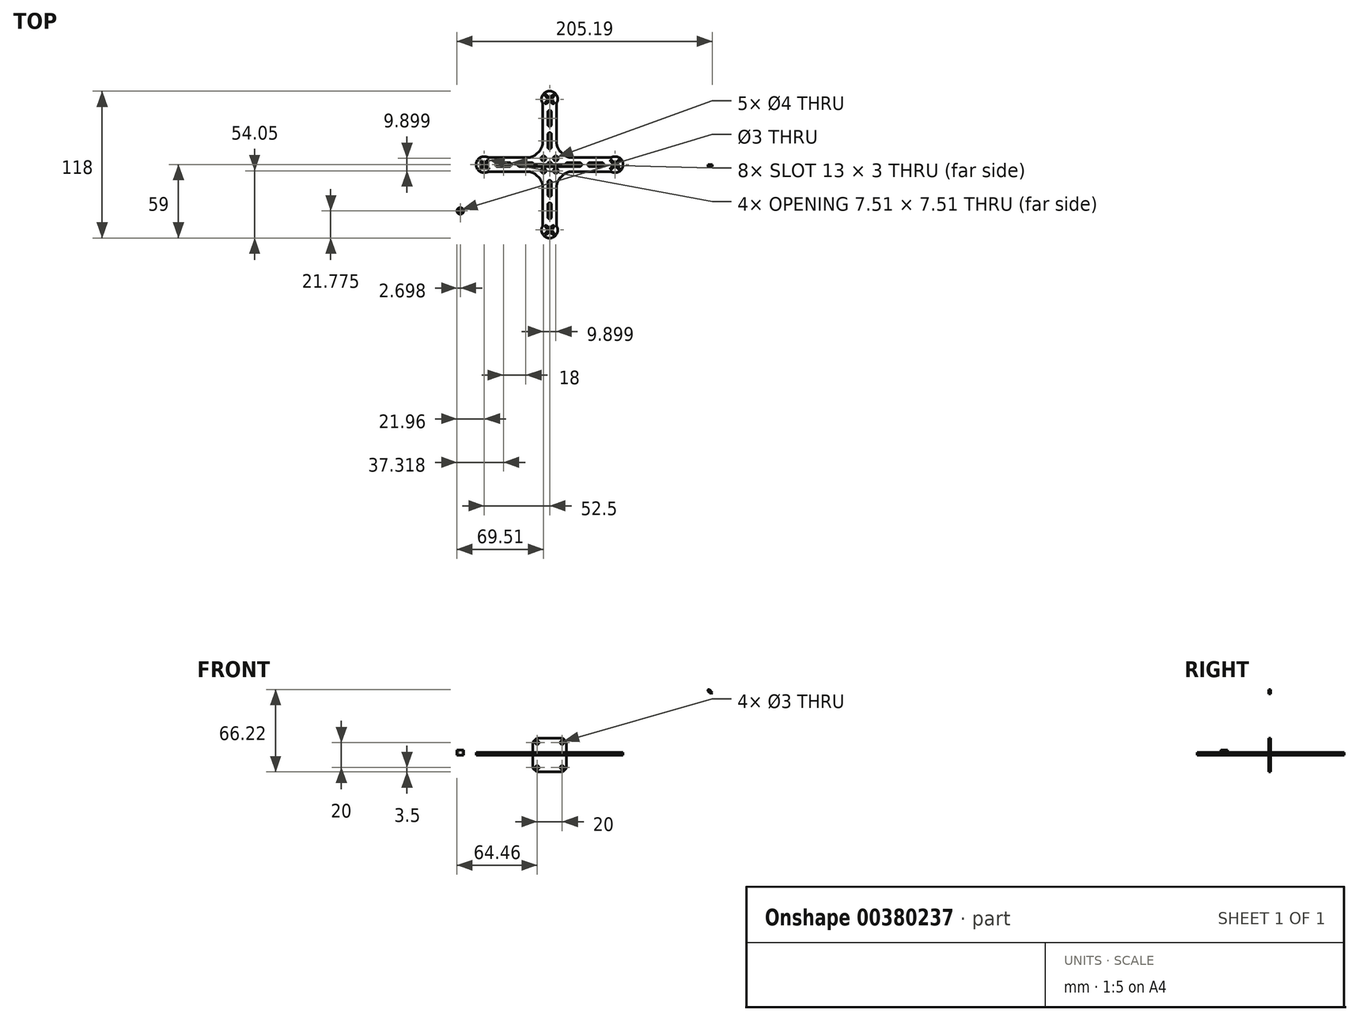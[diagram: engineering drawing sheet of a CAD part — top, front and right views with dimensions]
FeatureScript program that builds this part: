
annotation { "Feature Type Name" : "Feature", "Feature Type Description" : "" }
export const myFeature = defineFeature(function(context is Context, id is Id, definition is map)
    precondition{}
    {
        {
            var Q0;
            Q0=qCreatedBy(makeId("Front.planeOp"),FACE);
            var sketch = newSketch(context, id + "F0", { "sketchPlane" : qUnion([Q0])});
            skCircle(sketch, "E0", {"center": v(-10, 10) * mm, "radius": 1.5 * mm});
            skCircle(sketch, "E1.MirrorC", {"center": v(10, 10) * mm, "radius": 1.5 * mm});
            skCircle(sketch, "E2.MirrorC", {"center": v(-10, -10) * mm, "radius": 1.5 * mm});
            skCircle(sketch, "E3.MirrorC", {"center": v(10, -10) * mm, "radius": 1.5 * mm});
            skLineSegment(sketch, "E4", {"start": v(-13.5, 10.5) * mm, "end": v(-10.5, 13.5) * mm});
            skLineSegment(sketch, "E5", {"start": v(0, 3.77) * mm, "end": v(0, -2.66) * mm, "construction": true});
            skLineSegment(sketch, "E6", {"start": v(-3.53, 0) * mm, "end": v(2.6, 0) * mm, "construction": true});
            skLineSegment(sketch, "E7.MirrorCS", {"start": v(13.5, 10.5) * mm, "end": v(10.5, 13.5) * mm});
            skLineSegment(sketch, "E8.MirrorCS", {"start": v(13.5, -10.5) * mm, "end": v(10.5, -13.5) * mm});
            skLineSegment(sketch, "E9.MirrorCS", {"start": v(-13.5, -10.5) * mm, "end": v(-10.5, -13.5) * mm});
            skLineSegment(sketch, "E10", {"start": v(-13.5, 10.5) * mm, "end": v(-13.5, -10.5) * mm});
            skLineSegment(sketch, "E11", {"start": v(-10.5, 13.5) * mm, "end": v(10.5, 13.5) * mm});
            skLineSegment(sketch, "E12", {"start": v(13.5, 10.5) * mm, "end": v(13.5, -10.5) * mm});
            skLineSegment(sketch, "E13", {"start": v(10.5, -13.5) * mm, "end": v(-10.5, -13.5) * mm});
            skPoint(sketch, "E14.startSnap0", {"position": v(130.73, -3.54) * mm});
            skLineSegment(sketch, "E15", {"start": v(130.73, 48.96) * mm, "end": v(121.15, 39.38) * mm, "construction": true});
            skLineSegment(sketch, "E16", {"start": v(130.73, 48.96) * mm, "end": v(120.31, 59.39) * mm, "construction": true});
            skLineSegment(sketch, "E17", {"start": v(130.73, 48.96) * mm, "end": v(141.05, 59.28) * mm, "construction": true});
            skLineSegment(sketch, "E18", {"start": v(130.73, 48.96) * mm, "end": v(140.68, 39.01) * mm, "construction": true});
            skCircle(sketch, "E19", {"center": v(130.73, 48.96) * mm, "radius": 4.25 * mm, "construction": true});
            skLineSegment(sketch, "E20", {"start": v(128.26, 52.5) * mm, "end": v(134.27, 46.49) * mm});
            skLineSegment(sketch, "E21", {"start": v(127.2, 51.44) * mm, "end": v(133.2, 45.43) * mm});
            skLineSegment(sketch, "E22", {"start": v(127.2, 46.49) * mm, "end": v(133.16, 52.45) * mm});
            skLineSegment(sketch, "E23", {"start": v(134.27, 51.44) * mm, "end": v(128.26, 45.43) * mm});
            skArc(sketch, "E24", {"start": v(127.2, 51.44) * mm, "mid": v(127.2, 52.5) * mm, "end": v(128.26, 52.5) * mm});
            skArc(sketch, "E25", {"start": v(134.27, 46.49) * mm, "mid": v(134.27, 45.43) * mm, "end": v(133.2, 45.43) * mm});
            skArc(sketch, "E26", {"start": v(128.26, 45.43) * mm, "mid": v(127.2, 45.43) * mm, "end": v(127.2, 46.49) * mm});
            skArc(sketch, "E27", {"start": v(133.16, 52.45) * mm, "mid": v(134.24, 52.52) * mm, "end": v(134.27, 51.44) * mm});
            skLineSegment(sketch, "E28", {"start": v(130.73, 48.96) * mm, "end": v(121.92, 48.96) * mm, "construction": true});
            skLineSegment(sketch, "E29", {"start": v(130.73, 48.96) * mm, "end": v(139.92, 48.96) * mm, "construction": true});
            skLineSegment(sketch, "E30", {"start": v(130.73, -3.54) * mm, "end": v(147.32, 13.05) * mm, "construction": true});
            skLineSegment(sketch, "E31", {"start": v(130.73, -3.54) * mm, "end": v(114.8, -19.47) * mm, "construction": true});
            skLineSegment(sketch, "E32", {"start": v(130.73, -3.54) * mm, "end": v(113.54, 13.66) * mm, "construction": true});
            skLineSegment(sketch, "E33", {"start": v(130.73, -3.54) * mm, "end": v(149.26, -22.06) * mm, "construction": true});
            skPoint(sketch, "E34.centerSnap0", {"position": v(141.34, 7.07) * mm});
            skLineSegment(sketch, "E35", {"start": v(130.73, 35.6) * mm, "end": v(133.9, 35.6) * mm, "construction": true});
            skPoint(sketch, "E36.startSnap0", {"position": v(132.32, 35.6) * mm});
            skLineSegment(sketch, "E37", {"start": v(130.73, 10.6) * mm, "end": v(134.35, 10.6) * mm, "construction": true});
            skArc(sketch, "E38", {"start": v(132.23, 35.6) * mm, "mid": v(130.73, 37.1) * mm, "end": v(129.23, 35.6) * mm});
            skArc(sketch, "E39", {"start": v(132.23, 10.6) * mm, "mid": v(130.73, 9.1) * mm, "end": v(129.23, 10.6) * mm});
            skLineSegment(sketch, "E40", {"start": v(130.73, 48.96) * mm, "end": v(121.76, 43.79) * mm, "construction": true});
            skLineSegment(sketch, "E41.MirrorCS", {"start": v(130.73, 48.96) * mm, "end": v(139.7, 43.79) * mm, "construction": true});
            skLineSegment(sketch, "E42", {"start": v(136.36, 45.71) * mm, "end": v(137.16, 47.1) * mm, "construction": true});
            skArc(sketch, "E43", {"start": v(136.36, 45.71) * mm, "mid": v(130.73, 55.46) * mm, "end": v(125.1, 45.71) * mm});
            skLineSegment(sketch, "E44", {"start": v(125.1, 45.71) * mm, "end": v(125.1, 16.2) * mm});
            skLineSegment(sketch, "E45.MirrorCS", {"start": v(136.36, 45.71) * mm, "end": v(136.36, 16.2) * mm});
            skLineSegment(sketch, "E46.1.1", {"start": v(91.6, -5.04) * mm, "end": v(116.6, -5.04) * mm});
            skLineSegment(sketch, "E46.1.2", {"start": v(74.7, -6.01) * mm, "end": v(80.7, 0) * mm});
            skLineSegment(sketch, "E46.1.4", {"start": v(91.6, -2.04) * mm, "end": v(116.6, -2.04) * mm});
            skPoint(sketch, "E46.1.5", {"position": v(120.13, 7.07) * mm});
            skLineSegment(sketch, "E46.1.6", {"start": v(81.48, 2.1) * mm, "end": v(111, 2.1) * mm});
            skLineSegment(sketch, "E46.1.7", {"start": v(81.48, -9.16) * mm, "end": v(111, -9.16) * mm});
            skLineSegment(sketch, "E46.1.8", {"start": v(75.76, -7.07) * mm, "end": v(81.77, -1.06) * mm});
            skLineSegment(sketch, "E46.1.10", {"start": v(75.76, 0) * mm, "end": v(81.77, -6.01) * mm});
            skPoint(sketch, "E46.1.12", {"position": v(91.6, -1.95) * mm});
            skArc(sketch, "E46.1.14", {"start": v(81.48, 2.1) * mm, "mid": v(71.73, -3.54) * mm, "end": v(81.48, -9.16) * mm});
            skArc(sketch, "E46.1.20", {"start": v(74.75, -1.1) * mm, "mid": v(74.67, -0.02) * mm, "end": v(75.76, 0) * mm});
            skLineSegment(sketch, "E46.1.21", {"start": v(80.7, -7.07) * mm, "end": v(74.75, -1.1) * mm});
            skArc(sketch, "E46.1.22", {"start": v(116.6, -2.04) * mm, "mid": v(118.1, -3.54) * mm, "end": v(116.6, -5.04) * mm});
            skArc(sketch, "E46.1.23", {"start": v(81.77, -6.01) * mm, "mid": v(81.77, -7.07) * mm, "end": v(80.7, -7.07) * mm});
            skArc(sketch, "E46.1.24", {"start": v(75.76, -7.07) * mm, "mid": v(74.7, -7.07) * mm, "end": v(74.7, -6.01) * mm});
            skArc(sketch, "E46.1.26", {"start": v(91.6, -2.04) * mm, "mid": v(90.1, -3.54) * mm, "end": v(91.6, -5.04) * mm});
            skArc(sketch, "E46.1.27", {"start": v(80.7, 0) * mm, "mid": v(81.77, 0) * mm, "end": v(81.77, -1.06) * mm});
            skLineSegment(sketch, "E46.2.1", {"start": v(132.23, -42.68) * mm, "end": v(132.23, -17.68) * mm});
            skLineSegment(sketch, "E46.2.2", {"start": v(133.2, -59.57) * mm, "end": v(127.2, -53.56) * mm});
            skLineSegment(sketch, "E46.2.4", {"start": v(129.23, -42.68) * mm, "end": v(129.23, -17.68) * mm});
            skPoint(sketch, "E46.2.5", {"position": v(120.13, -14.14) * mm});
            skLineSegment(sketch, "E46.2.6", {"start": v(125.1, -52.79) * mm, "end": v(125.1, -23.26) * mm});
            skLineSegment(sketch, "E46.2.7", {"start": v(136.36, -52.79) * mm, "end": v(136.36, -23.26) * mm});
            skLineSegment(sketch, "E46.2.8", {"start": v(134.27, -58.51) * mm, "end": v(128.26, -52.5) * mm});
            skLineSegment(sketch, "E46.2.10", {"start": v(127.2, -58.51) * mm, "end": v(133.2, -52.5) * mm});
            skPoint(sketch, "E46.2.12", {"position": v(129.15, -42.68) * mm});
            skArc(sketch, "E46.2.14", {"start": v(125.1, -52.79) * mm, "mid": v(130.73, -62.54) * mm, "end": v(136.36, -52.79) * mm});
            skArc(sketch, "E46.2.20", {"start": v(128.3, -59.52) * mm, "mid": v(127.22, -59.6) * mm, "end": v(127.2, -58.51) * mm});
            skLineSegment(sketch, "E46.2.21", {"start": v(134.27, -53.56) * mm, "end": v(128.3, -59.52) * mm});
            skArc(sketch, "E46.2.22", {"start": v(129.23, -17.68) * mm, "mid": v(130.73, -16.18) * mm, "end": v(132.23, -17.68) * mm});
            skArc(sketch, "E46.2.23", {"start": v(133.2, -52.5) * mm, "mid": v(134.27, -52.5) * mm, "end": v(134.27, -53.56) * mm});
            skArc(sketch, "E46.2.24", {"start": v(134.27, -58.51) * mm, "mid": v(134.27, -59.57) * mm, "end": v(133.2, -59.57) * mm});
            skArc(sketch, "E46.2.26", {"start": v(129.23, -42.68) * mm, "mid": v(130.73, -44.18) * mm, "end": v(132.23, -42.68) * mm});
            skArc(sketch, "E46.2.27", {"start": v(127.2, -53.56) * mm, "mid": v(127.2, -52.5) * mm, "end": v(128.26, -52.5) * mm});
            skLineSegment(sketch, "E46.3.1", {"start": v(169.88, -2.04) * mm, "end": v(144.88, -2.04) * mm});
            skLineSegment(sketch, "E46.3.2", {"start": v(186.77, -1.06) * mm, "end": v(180.76, -7.07) * mm});
            skLineSegment(sketch, "E46.3.4", {"start": v(169.88, -5.04) * mm, "end": v(144.88, -5.04) * mm});
            skPoint(sketch, "E46.3.5", {"position": v(141.34, -14.14) * mm});
            skLineSegment(sketch, "E46.3.6", {"start": v(179.98, -9.16) * mm, "end": v(150.46, -9.16) * mm});
            skLineSegment(sketch, "E46.3.7", {"start": v(179.98, 2.1) * mm, "end": v(150.46, 2.1) * mm});
            skLineSegment(sketch, "E46.3.8", {"start": v(185.7, 0) * mm, "end": v(179.7, -6.01) * mm});
            skLineSegment(sketch, "E46.3.10", {"start": v(185.7, -7.07) * mm, "end": v(179.7, -1.06) * mm});
            skPoint(sketch, "E46.3.12", {"position": v(169.88, -5.12) * mm});
            skArc(sketch, "E46.3.14", {"start": v(179.98, -9.16) * mm, "mid": v(189.73, -3.54) * mm, "end": v(179.98, 2.1) * mm});
            skArc(sketch, "E46.3.20", {"start": v(186.72, -5.97) * mm, "mid": v(186.8, -7.05) * mm, "end": v(185.7, -7.07) * mm});
            skLineSegment(sketch, "E46.3.21", {"start": v(180.76, 0) * mm, "end": v(186.72, -5.97) * mm});
            skArc(sketch, "E46.3.22", {"start": v(144.88, -5.04) * mm, "mid": v(143.38, -3.54) * mm, "end": v(144.88, -2.04) * mm});
            skArc(sketch, "E46.3.23", {"start": v(179.7, -1.06) * mm, "mid": v(179.7, 0) * mm, "end": v(180.76, 0) * mm});
            skArc(sketch, "E46.3.24", {"start": v(185.7, 0) * mm, "mid": v(186.77, 0) * mm, "end": v(186.77, -1.06) * mm});
            skArc(sketch, "E46.3.26", {"start": v(169.88, -5.04) * mm, "mid": v(171.38, -3.54) * mm, "end": v(169.88, -2.04) * mm});
            skArc(sketch, "E46.3.27", {"start": v(180.76, -7.07) * mm, "mid": v(179.7, -7.07) * mm, "end": v(179.7, -6.01) * mm});
            skLineSegment(sketch, "E47", {"start": v(122.18, 9.12) * mm, "end": v(118.08, 5.02) * mm});
            skLineSegment(sketch, "E48", {"start": v(118.08, -12.1) * mm, "end": v(122.18, -16.2) * mm});
            skLineSegment(sketch, "E49", {"start": v(139.3, -16.2) * mm, "end": v(143.39, -12.1) * mm});
            skLineSegment(sketch, "E50", {"start": v(143.39, 5.02) * mm, "end": v(139.3, 9.12) * mm});
            skArc(sketch, "E51.filletArc", {"start": v(122.18, 9.12) * mm, "mid": v(124.34, 12.36) * mm, "end": v(125.1, 16.2) * mm});
            skPoint(sketch, "E52.visualSharp", {"position": v(115.15, 2.1) * mm});
            skArc(sketch, "E52.filletArc", {"start": v(111, 2.1) * mm, "mid": v(114.83, 2.85) * mm, "end": v(118.08, 5.02) * mm});
            skPoint(sketch, "E53.visualSharp", {"position": v(136.36, 12.05) * mm});
            skArc(sketch, "E53.filletArc", {"start": v(136.36, 16.2) * mm, "mid": v(137.12, 12.36) * mm, "end": v(139.3, 9.12) * mm});
            skArc(sketch, "E54.filletArc", {"start": v(143.39, 5.02) * mm, "mid": v(146.63, 2.85) * mm, "end": v(150.46, 2.1) * mm});
            skPoint(sketch, "E55.visualSharp", {"position": v(146.32, -9.16) * mm});
            skArc(sketch, "E55.filletArc", {"start": v(150.46, -9.16) * mm, "mid": v(146.63, -9.93) * mm, "end": v(143.39, -12.1) * mm});
            skArc(sketch, "E56.filletArc", {"start": v(139.3, -16.2) * mm, "mid": v(137.12, -19.43) * mm, "end": v(136.36, -23.26) * mm});
            skPoint(sketch, "E57.visualSharp", {"position": v(125.1, -19.12) * mm});
            skArc(sketch, "E57.filletArc", {"start": v(125.1, -23.26) * mm, "mid": v(124.34, -19.43) * mm, "end": v(122.18, -16.2) * mm});
            skArc(sketch, "E58.filletArc", {"start": v(118.08, -12.1) * mm, "mid": v(114.83, -9.93) * mm, "end": v(111, -9.16) * mm});
            skCircle(sketch, "E59", {"center": v(130.73, -3.54) * mm, "radius": 2 * mm});
            skCircle(sketch, "E60", {"center": v(136.39, 2.12) * mm, "radius": 2 * mm});
            skCircle(sketch, "E61.MirrorC", {"center": v(125.08, -9.2) * mm, "radius": 2 * mm});
            skLineSegment(sketch, "E62", {"start": v(130.73, -3.54) * mm, "end": v(130.73, 5.88) * mm, "construction": true});
            skCircle(sketch, "E63.MirrorC", {"center": v(125.08, 2.12) * mm, "radius": 2 * mm});
            skCircle(sketch, "E64.MirrorC", {"center": v(136.39, -9.2) * mm, "radius": 2 * mm});
            skLineSegment(sketch, "E65", {"start": v(129.23, 35.6) * mm, "end": v(129.23, 27.6) * mm});
            skLineSegment(sketch, "E66", {"start": v(132.23, 27.6) * mm, "end": v(132.23, 35.6) * mm});
            skLineSegment(sketch, "E67", {"start": v(129.23, 10.6) * mm, "end": v(129.23, 18.6) * mm});
            skLineSegment(sketch, "E68", {"start": v(132.23, 18.6) * mm, "end": v(132.23, 10.6) * mm});
            skArc(sketch, "E69", {"start": v(129.23, 18.6) * mm, "mid": v(130.73, 20.1) * mm, "end": v(132.23, 18.6) * mm});
            skArc(sketch, "E70", {"start": v(129.23, 27.6) * mm, "mid": v(130.73, 26.1) * mm, "end": v(132.23, 27.6) * mm});
            skCircle(sketch, "E71", {"center": v(252.65, 46.38) * mm, "radius": 4.25 * mm, "construction": true});
            skLineSegment(sketch, "E72", {"start": v(245.3, 46.38) * mm, "end": v(259.84, 46.38) * mm, "construction": true});
            skLineSegment(sketch, "E73", {"start": v(252.65, 46.38) * mm, "end": v(246.48, 40.2) * mm, "construction": true});
            skLineSegment(sketch, "E74", {"start": v(252.65, 46.38) * mm, "end": v(258.2, 51.93) * mm, "construction": true});
            skLineSegment(sketch, "E75.MirrorCS", {"start": v(252.65, 46.38) * mm, "end": v(247.1, 51.93) * mm, "construction": true});
            skLineSegment(sketch, "E76", {"start": v(254.27, 49.06) * mm, "end": v(249.97, 44.76) * mm, "construction": true});
            skLineSegment(sketch, "E77", {"start": v(249.65, 49.38) * mm, "end": v(248.95, 48.68) * mm, "construction": true});
            skLineSegment(sketch, "E78", {"start": v(249.12, 48.85) * mm, "end": v(251.6, 46.38) * mm});
            skLineSegment(sketch, "E79.MirrorCS", {"start": v(250.18, 49.91) * mm, "end": v(252.65, 47.44) * mm});
            skArc(sketch, "E80", {"start": v(249.12, 48.85) * mm, "mid": v(249.12, 49.91) * mm, "end": v(250.18, 49.91) * mm});
            skArc(sketch, "E81.1.0", {"start": v(250.18, 42.84) * mm, "mid": v(249.12, 42.84) * mm, "end": v(249.12, 43.9) * mm});
            skLineSegment(sketch, "E81.1.1", {"start": v(249.12, 43.9) * mm, "end": v(251.6, 46.38) * mm});
            skLineSegment(sketch, "E81.1.2", {"start": v(250.18, 42.84) * mm, "end": v(252.65, 45.32) * mm});
            skArc(sketch, "E81.2.0", {"start": v(256.19, 43.9) * mm, "mid": v(256.19, 42.84) * mm, "end": v(255.13, 42.84) * mm});
            skLineSegment(sketch, "E81.2.1", {"start": v(255.13, 42.84) * mm, "end": v(252.65, 45.32) * mm});
            skLineSegment(sketch, "E81.2.2", {"start": v(256.19, 43.9) * mm, "end": v(253.71, 46.38) * mm});
            skArc(sketch, "E81.3.0", {"start": v(255.13, 49.91) * mm, "mid": v(256.19, 49.91) * mm, "end": v(256.19, 48.85) * mm});
            skLineSegment(sketch, "E81.3.1", {"start": v(256.19, 48.85) * mm, "end": v(253.71, 46.38) * mm});
            skLineSegment(sketch, "E81.3.2", {"start": v(255.13, 49.91) * mm, "end": v(252.65, 47.44) * mm});
            skLineSegment(sketch, "E82", {"start": v(252.65, 46.38) * mm, "end": v(246.46, 42.8) * mm, "construction": true});
            skLineSegment(sketch, "E83.MirrorCS", {"start": v(252.65, 46.38) * mm, "end": v(258.84, 42.8) * mm, "construction": true});
            skArc(sketch, "E84", {"start": v(247.02, 43.13) * mm, "mid": v(252.65, 52.88) * mm, "end": v(258.28, 43.13) * mm});
            skCircle(sketch, "E85", {"center": v(252.65, -6.12) * mm, "radius": 2 * mm});
            skLineSegment(sketch, "E86", {"start": v(252.65, 57.43) * mm, "end": v(252.65, -10.81) * mm, "construction": true});
            skCircle(sketch, "E87", {"center": v(252.65, 8.02) * mm, "radius": 1.5 * mm, "construction": true});
            skCircle(sketch, "E88", {"center": v(252.65, 36.02) * mm, "radius": 1.5 * mm, "construction": true});
            skCircle(sketch, "E89", {"center": v(252.65, 26.02) * mm, "radius": 1.5 * mm, "construction": true});
            skCircle(sketch, "E90", {"center": v(252.65, 18.02) * mm, "radius": 1.5 * mm, "construction": true});
            skLineSegment(sketch, "E91", {"start": v(251.15, 18.02) * mm, "end": v(251.15, 8.02) * mm});
            skLineSegment(sketch, "E92", {"start": v(254.15, 18.02) * mm, "end": v(254.15, 8.02) * mm});
            skArc(sketch, "E93", {"start": v(251.15, 8.02) * mm, "mid": v(252.65, 6.52) * mm, "end": v(254.15, 8.02) * mm});
            skArc(sketch, "E94", {"start": v(251.15, 18.02) * mm, "mid": v(252.65, 19.52) * mm, "end": v(254.15, 18.02) * mm});
            skLineSegment(sketch, "E95", {"start": v(251.15, 26.02) * mm, "end": v(251.15, 36.02) * mm});
            skLineSegment(sketch, "E96", {"start": v(254.15, 36.02) * mm, "end": v(254.15, 26.02) * mm});
            skArc(sketch, "E97", {"start": v(251.15, 26.02) * mm, "mid": v(252.65, 24.52) * mm, "end": v(254.15, 26.02) * mm});
            skArc(sketch, "E98", {"start": v(251.15, 36.02) * mm, "mid": v(252.65, 37.52) * mm, "end": v(254.15, 36.02) * mm});
            skLineSegment(sketch, "E99", {"start": v(252.65, -6.12) * mm, "end": v(265.9, 7.13) * mm, "construction": true});
            skLineSegment(sketch, "E100", {"start": v(252.65, -6.12) * mm, "end": v(239.95, -18.82) * mm, "construction": true});
            skLineSegment(sketch, "E101.MirrorCS", {"start": v(252.65, -6.12) * mm, "end": v(239.4, 7.13) * mm, "construction": true});
            skLineSegment(sketch, "E102.MirrorCS", {"start": v(252.65, -6.12) * mm, "end": v(265.35, -18.82) * mm, "construction": true});
            skSolve(sketch);
        }
        {
            var Q0;
            Q0=makeQuery(id+"F0.imprint","IMPRINT",FACE,{"disambiguationData":[TD([[makeQuery(id+"F0.imprint","IMPRINT",EDGE,{"derivedFrom":sQuery(id+"F0.wireOp",EDGE,"E0")}),-1.0]])]});
            var Q1;
            {var subQ28=sQuery(id+"F0.wireOp",EDGE,"E24");Q1=makeQuery(id+"F0.imprint","IMPRINT",FACE,{"disambiguationData":[TD([[makeQuery(id+"F0.imprint","IMPRINT",EDGE,{"derivedFrom":subQ28}),1.0]])]});}
            extrude(context, id + "F1", {"entities" : qUnion([Q0, Q1]), "depth" : 1.5 * mm});
        }
        {
            var Q0;
            Q0=qCreatedBy(makeId("Top.planeOp"),FACE);
            var sketch = newSketch(context, id + "F2", { "sketchPlane" : qUnion([Q0])});
            skCircle(sketch, "E103", {"center": v(0, 52.5) * mm, "radius": 4.25 * mm, "construction": true});
            skLineSegment(sketch, "E104", {"start": v(-7.35, 52.5) * mm, "end": v(7.2, 52.5) * mm, "construction": true});
            skLineSegment(sketch, "E105", {"start": v(0, 52.5) * mm, "end": v(-6.17, 46.33) * mm, "construction": true});
            skLineSegment(sketch, "E106", {"start": v(0, 52.5) * mm, "end": v(5.55, 58.05) * mm, "construction": true});
            skLineSegment(sketch, "E107.MirrorCS", {"start": v(0, 52.5) * mm, "end": v(-5.55, 58.05) * mm, "construction": true});
            skLineSegment(sketch, "E108", {"start": v(-3, 55.5) * mm, "end": v(-3.7, 54.8) * mm, "construction": true});
            skLineSegment(sketch, "E109", {"start": v(-3.54, 54.97) * mm, "end": v(-1.06, 52.5) * mm});
            skLineSegment(sketch, "E110.MirrorCS", {"start": v(-2.47, 56.04) * mm, "end": v(0, 53.56) * mm});
            skArc(sketch, "E111", {"start": v(-3.54, 54.97) * mm, "mid": v(-3.54, 56.04) * mm, "end": v(-2.47, 56.04) * mm});
            skArc(sketch, "E112.1.0", {"start": v(-2.47, 48.96) * mm, "mid": v(-3.54, 48.96) * mm, "end": v(-3.54, 50.03) * mm});
            skLineSegment(sketch, "E112.1.1", {"start": v(-3.54, 50.03) * mm, "end": v(-1.06, 52.5) * mm});
            skLineSegment(sketch, "E112.1.2", {"start": v(-2.47, 48.96) * mm, "end": v(0, 51.44) * mm});
            skArc(sketch, "E112.2.0", {"start": v(3.54, 50.03) * mm, "mid": v(3.54, 48.96) * mm, "end": v(2.47, 48.96) * mm});
            skLineSegment(sketch, "E112.2.1", {"start": v(2.47, 48.96) * mm, "end": v(0, 51.44) * mm});
            skLineSegment(sketch, "E112.2.2", {"start": v(3.54, 50.03) * mm, "end": v(1.06, 52.5) * mm});
            skArc(sketch, "E112.3.0", {"start": v(2.47, 56.04) * mm, "mid": v(3.54, 56.04) * mm, "end": v(3.54, 54.97) * mm});
            skLineSegment(sketch, "E112.3.1", {"start": v(3.54, 54.97) * mm, "end": v(1.06, 52.5) * mm});
            skLineSegment(sketch, "E112.3.2", {"start": v(2.47, 56.04) * mm, "end": v(0, 53.56) * mm});
            skLineSegment(sketch, "E113", {"start": v(0, 52.5) * mm, "end": v(-6.19, 48.93) * mm, "construction": true});
            skLineSegment(sketch, "E114.MirrorCS", {"start": v(0, 52.5) * mm, "end": v(6.19, 48.93) * mm, "construction": true});
            skArc(sketch, "E115", {"start": v(-5.63, 49.25) * mm, "mid": v(0, 59) * mm, "end": v(5.63, 49.25) * mm});
            skCircle(sketch, "E116", {"center": v(0, 0) * mm, "radius": 2 * mm});
            skLineSegment(sketch, "E117", {"start": v(0, 65.69) * mm, "end": v(0, -2.55) * mm, "construction": true});
            skLineSegment(sketch, "E118", {"start": v(-1.5, 24.14) * mm, "end": v(-1.5, 14.14) * mm});
            skLineSegment(sketch, "E119", {"start": v(1.5, 24.14) * mm, "end": v(1.5, 14.14) * mm});
            skArc(sketch, "E120", {"start": v(-1.5, 14.14) * mm, "mid": v(0, 12.64) * mm, "end": v(1.5, 14.14) * mm});
            skArc(sketch, "E121", {"start": v(-1.5, 24.14) * mm, "mid": v(0, 25.64) * mm, "end": v(1.5, 24.14) * mm});
            skLineSegment(sketch, "E122", {"start": v(-1.5, 32.14) * mm, "end": v(-1.5, 42.14) * mm});
            skLineSegment(sketch, "E123", {"start": v(1.5, 42.14) * mm, "end": v(1.5, 32.14) * mm});
            skArc(sketch, "E124", {"start": v(-1.5, 32.14) * mm, "mid": v(0, 30.64) * mm, "end": v(1.5, 32.14) * mm});
            skArc(sketch, "E125", {"start": v(-1.5, 42.14) * mm, "mid": v(0, 43.64) * mm, "end": v(1.5, 42.14) * mm});
            skLineSegment(sketch, "E126", {"start": v(0, 0) * mm, "end": v(13.25, 13.25) * mm, "construction": true});
            skLineSegment(sketch, "E127", {"start": v(0, 0) * mm, "end": v(-12.7, -12.7) * mm, "construction": true});
            skLineSegment(sketch, "E128.MirrorCS", {"start": v(0, 0) * mm, "end": v(-13.25, 13.25) * mm, "construction": true});
            skLineSegment(sketch, "E129.MirrorCS", {"start": v(0, 0) * mm, "end": v(12.7, -12.7) * mm, "construction": true});
            skCircle(sketch, "E130", {"center": v(4.95, 4.95) * mm, "radius": 2 * mm});
            skCircle(sketch, "E131.MirrorC", {"center": v(-4.95, 4.95) * mm, "radius": 2 * mm});
            skCircle(sketch, "E132.MirrorC", {"center": v(4.95, -4.95) * mm, "radius": 2 * mm});
            skCircle(sketch, "E133.MirrorC", {"center": v(-4.95, -4.95) * mm, "radius": 2 * mm});
            skLineSegment(sketch, "E134", {"start": v(-5.63, 49.25) * mm, "end": v(-5.63, 17.6) * mm});
            skLineSegment(sketch, "E135", {"start": v(5.63, 49.25) * mm, "end": v(5.63, 17.6) * mm});
            skCircle(sketch, "E136", {"center": v(-380.04, 55.3) * mm, "radius": 4.25 * mm, "construction": true});
            skLineSegment(sketch, "E137", {"start": v(-387.39, 55.3) * mm, "end": v(-372.84, 55.3) * mm, "construction": true});
            skLineSegment(sketch, "E138", {"start": v(-380.04, 55.3) * mm, "end": v(-386.2, 49.13) * mm, "construction": true});
            skLineSegment(sketch, "E139", {"start": v(-380.04, 55.3) * mm, "end": v(-374.48, 60.86) * mm, "construction": true});
            skLineSegment(sketch, "E140.MirrorCS", {"start": v(-380.04, 55.3) * mm, "end": v(-385.59, 60.86) * mm, "construction": true});
            skLineSegment(sketch, "E141", {"start": v(-378.42, 57.98) * mm, "end": v(-382.72, 53.68) * mm, "construction": true});
            skLineSegment(sketch, "E142", {"start": v(-383.04, 58.3) * mm, "end": v(-383.74, 57.6) * mm, "construction": true});
            skLineSegment(sketch, "E143", {"start": v(-383.57, 57.78) * mm, "end": v(-381.1, 55.3) * mm});
            skLineSegment(sketch, "E144.MirrorCS", {"start": v(-382.51, 58.84) * mm, "end": v(-380.04, 56.36) * mm});
            skArc(sketch, "E145", {"start": v(-383.57, 57.78) * mm, "mid": v(-383.57, 58.84) * mm, "end": v(-382.51, 58.84) * mm});
            skArc(sketch, "E146.1.0", {"start": v(-382.51, 51.77) * mm, "mid": v(-383.57, 51.77) * mm, "end": v(-383.57, 52.83) * mm});
            skLineSegment(sketch, "E146.1.1", {"start": v(-383.57, 52.83) * mm, "end": v(-381.1, 55.3) * mm});
            skLineSegment(sketch, "E146.1.2", {"start": v(-382.51, 51.77) * mm, "end": v(-380.04, 54.24) * mm});
            skArc(sketch, "E146.2.0", {"start": v(-376.5, 52.83) * mm, "mid": v(-376.5, 51.77) * mm, "end": v(-377.56, 51.77) * mm});
            skLineSegment(sketch, "E146.2.1", {"start": v(-377.56, 51.77) * mm, "end": v(-380.04, 54.24) * mm});
            skLineSegment(sketch, "E146.2.2", {"start": v(-376.5, 52.83) * mm, "end": v(-378.98, 55.3) * mm});
            skArc(sketch, "E146.3.0", {"start": v(-377.56, 58.84) * mm, "mid": v(-376.5, 58.84) * mm, "end": v(-376.5, 57.78) * mm});
            skLineSegment(sketch, "E146.3.1", {"start": v(-376.5, 57.78) * mm, "end": v(-378.98, 55.3) * mm});
            skLineSegment(sketch, "E146.3.2", {"start": v(-377.56, 58.84) * mm, "end": v(-380.04, 56.36) * mm});
            skLineSegment(sketch, "E147", {"start": v(-380.04, 55.3) * mm, "end": v(-386.22, 51.73) * mm, "construction": true});
            skLineSegment(sketch, "E148.MirrorCS", {"start": v(-380.04, 55.3) * mm, "end": v(-373.85, 51.73) * mm, "construction": true});
            skArc(sketch, "E149", {"start": v(-385.66, 52.05) * mm, "mid": v(-380.04, 61.8) * mm, "end": v(-374.4, 52.05) * mm});
            skCircle(sketch, "E150", {"center": v(-380.04, 2.8) * mm, "radius": 2 * mm});
            skLineSegment(sketch, "E151", {"start": v(-380.04, 68.5) * mm, "end": v(-380.04, 0.25) * mm, "construction": true});
            skCircle(sketch, "E152", {"center": v(-380.04, 16.95) * mm, "radius": 1.5 * mm, "construction": true});
            skCircle(sketch, "E153", {"center": v(-380.04, 44.95) * mm, "radius": 1.5 * mm, "construction": true});
            skCircle(sketch, "E154", {"center": v(-380.04, 34.95) * mm, "radius": 1.5 * mm, "construction": true});
            skCircle(sketch, "E155", {"center": v(-380.04, 26.95) * mm, "radius": 1.5 * mm, "construction": true});
            skLineSegment(sketch, "E156", {"start": v(-381.54, 26.95) * mm, "end": v(-381.54, 16.95) * mm});
            skLineSegment(sketch, "E157", {"start": v(-378.54, 26.95) * mm, "end": v(-378.54, 16.95) * mm});
            skArc(sketch, "E158", {"start": v(-381.54, 16.95) * mm, "mid": v(-380.04, 15.45) * mm, "end": v(-378.54, 16.95) * mm});
            skArc(sketch, "E159", {"start": v(-381.54, 26.95) * mm, "mid": v(-380.04, 28.45) * mm, "end": v(-378.54, 26.95) * mm});
            skLineSegment(sketch, "E160", {"start": v(-381.54, 34.95) * mm, "end": v(-381.54, 44.95) * mm});
            skLineSegment(sketch, "E161", {"start": v(-378.54, 44.95) * mm, "end": v(-378.54, 34.95) * mm});
            skArc(sketch, "E162", {"start": v(-381.54, 34.95) * mm, "mid": v(-380.04, 33.45) * mm, "end": v(-378.54, 34.95) * mm});
            skArc(sketch, "E163", {"start": v(-381.54, 44.95) * mm, "mid": v(-380.04, 46.45) * mm, "end": v(-378.54, 44.95) * mm});
            skLineSegment(sketch, "E164", {"start": v(-380.04, 2.8) * mm, "end": v(-366.78, 16.06) * mm, "construction": true});
            skLineSegment(sketch, "E165", {"start": v(-380.04, 2.8) * mm, "end": v(-392.74, -9.9) * mm, "construction": true});
            skLineSegment(sketch, "E166.MirrorCS", {"start": v(-380.04, 2.8) * mm, "end": v(-393.29, 16.06) * mm, "construction": true});
            skLineSegment(sketch, "E167.MirrorCS", {"start": v(-380.04, 2.8) * mm, "end": v(-367.34, -9.9) * mm, "construction": true});
            skCircle(sketch, "E168", {"center": v(-372.96, 9.87) * mm, "radius": 2 * mm});
            skCircle(sketch, "E169.MirrorC", {"center": v(-387.1, 9.87) * mm, "radius": 2 * mm});
            skCircle(sketch, "E170.MirrorC", {"center": v(-372.96, -4.27) * mm, "radius": 2 * mm});
            skCircle(sketch, "E171.MirrorC", {"center": v(-387.1, -4.27) * mm, "radius": 2 * mm});
            skLineSegment(sketch, "E172", {"start": v(-360.94, 2.8) * mm, "end": v(-380.04, -16.29) * mm, "construction": true});
            skLineSegment(sketch, "E173", {"start": v(-380.04, -16.29) * mm, "end": v(-399.13, 2.8) * mm, "construction": true});
            skLineSegment(sketch, "E174", {"start": v(-399.13, 2.8) * mm, "end": v(-380.04, 21.9) * mm, "construction": true});
            skLineSegment(sketch, "E175", {"start": v(-380.04, 21.9) * mm, "end": v(-360.94, 2.8) * mm, "construction": true});
            skLineSegment(sketch, "E176", {"start": v(-385.66, 52.05) * mm, "end": v(-385.66, 16.27) * mm});
            skLineSegment(sketch, "E177", {"start": v(-374.4, 52.05) * mm, "end": v(-374.4, 16.27) * mm});
            skLineSegment(sketch, "E178.1.0", {"start": v(-49.25, -5.63) * mm, "end": v(-17.6, -5.63) * mm});
            skArc(sketch, "E178.1.1", {"start": v(-49.25, -5.63) * mm, "mid": v(-59, 0) * mm, "end": v(-49.25, 5.63) * mm});
            skLineSegment(sketch, "E178.1.2", {"start": v(-49.25, 5.63) * mm, "end": v(-17.6, 5.63) * mm});
            skArc(sketch, "E178.1.3", {"start": v(-42.14, -1.5) * mm, "mid": v(-43.64, 0) * mm, "end": v(-42.14, 1.5) * mm});
            skLineSegment(sketch, "E178.1.4", {"start": v(-42.14, 1.5) * mm, "end": v(-32.14, 1.5) * mm});
            skLineSegment(sketch, "E178.1.5", {"start": v(-32.14, -1.5) * mm, "end": v(-42.14, -1.5) * mm});
            skArc(sketch, "E178.1.6", {"start": v(-32.14, -1.5) * mm, "mid": v(-30.64, 0) * mm, "end": v(-32.14, 1.5) * mm});
            skArc(sketch, "E178.1.7", {"start": v(-54.97, -3.54) * mm, "mid": v(-56.04, -3.54) * mm, "end": v(-56.04, -2.47) * mm});
            skLineSegment(sketch, "E178.1.8", {"start": v(-56.04, -2.47) * mm, "end": v(-53.56, 0) * mm});
            skLineSegment(sketch, "E178.1.9", {"start": v(-54.97, -3.54) * mm, "end": v(-52.5, -1.06) * mm});
            skLineSegment(sketch, "E178.1.10", {"start": v(-56.04, 2.47) * mm, "end": v(-53.56, 0) * mm});
            skLineSegment(sketch, "E178.1.11", {"start": v(-54.97, 3.54) * mm, "end": v(-52.5, 1.06) * mm});
            skArc(sketch, "E178.1.12", {"start": v(-56.04, 2.47) * mm, "mid": v(-56.04, 3.54) * mm, "end": v(-54.97, 3.54) * mm});
            skLineSegment(sketch, "E178.1.13", {"start": v(-50.03, 3.54) * mm, "end": v(-52.5, 1.06) * mm});
            skLineSegment(sketch, "E178.1.14", {"start": v(-48.96, 2.47) * mm, "end": v(-51.44, 0) * mm});
            skArc(sketch, "E178.1.15", {"start": v(-50.03, 3.54) * mm, "mid": v(-48.96, 3.54) * mm, "end": v(-48.96, 2.47) * mm});
            skArc(sketch, "E178.1.16", {"start": v(-48.96, -2.47) * mm, "mid": v(-48.96, -3.54) * mm, "end": v(-50.03, -3.54) * mm});
            skLineSegment(sketch, "E178.1.17", {"start": v(-48.96, -2.47) * mm, "end": v(-51.44, 0) * mm});
            skLineSegment(sketch, "E178.1.18", {"start": v(-50.03, -3.54) * mm, "end": v(-52.5, -1.06) * mm});
            skLineSegment(sketch, "E178.1.19", {"start": v(-24.14, 1.5) * mm, "end": v(-14.14, 1.5) * mm});
            skArc(sketch, "E178.1.20", {"start": v(-24.14, -1.5) * mm, "mid": v(-25.64, 0) * mm, "end": v(-24.14, 1.5) * mm});
            skLineSegment(sketch, "E178.1.21", {"start": v(-24.14, -1.5) * mm, "end": v(-14.14, -1.5) * mm});
            skArc(sketch, "E178.1.22", {"start": v(-14.14, -1.5) * mm, "mid": v(-12.64, 0) * mm, "end": v(-14.14, 1.5) * mm});
            skLineSegment(sketch, "E178.2.0", {"start": v(5.63, -49.25) * mm, "end": v(5.63, -17.6) * mm});
            skArc(sketch, "E178.2.1", {"start": v(5.63, -49.25) * mm, "mid": v(0, -59) * mm, "end": v(-5.63, -49.25) * mm});
            skLineSegment(sketch, "E178.2.2", {"start": v(-5.63, -49.25) * mm, "end": v(-5.63, -17.6) * mm});
            skArc(sketch, "E178.2.3", {"start": v(1.5, -42.14) * mm, "mid": v(0, -43.64) * mm, "end": v(-1.5, -42.14) * mm});
            skLineSegment(sketch, "E178.2.4", {"start": v(-1.5, -42.14) * mm, "end": v(-1.5, -32.14) * mm});
            skLineSegment(sketch, "E178.2.5", {"start": v(1.5, -32.14) * mm, "end": v(1.5, -42.14) * mm});
            skArc(sketch, "E178.2.6", {"start": v(1.5, -32.14) * mm, "mid": v(0, -30.64) * mm, "end": v(-1.5, -32.14) * mm});
            skArc(sketch, "E178.2.7", {"start": v(3.54, -54.97) * mm, "mid": v(3.54, -56.04) * mm, "end": v(2.47, -56.04) * mm});
            skLineSegment(sketch, "E178.2.8", {"start": v(2.47, -56.04) * mm, "end": v(0, -53.56) * mm});
            skLineSegment(sketch, "E178.2.9", {"start": v(3.54, -54.97) * mm, "end": v(1.06, -52.5) * mm});
            skLineSegment(sketch, "E178.2.10", {"start": v(-2.47, -56.04) * mm, "end": v(0, -53.56) * mm});
            skLineSegment(sketch, "E178.2.11", {"start": v(-3.54, -54.97) * mm, "end": v(-1.06, -52.5) * mm});
            skArc(sketch, "E178.2.12", {"start": v(-2.47, -56.04) * mm, "mid": v(-3.54, -56.04) * mm, "end": v(-3.54, -54.97) * mm});
            skLineSegment(sketch, "E178.2.13", {"start": v(-3.54, -50.03) * mm, "end": v(-1.06, -52.5) * mm});
            skLineSegment(sketch, "E178.2.14", {"start": v(-2.47, -48.96) * mm, "end": v(0, -51.44) * mm});
            skArc(sketch, "E178.2.15", {"start": v(-3.54, -50.03) * mm, "mid": v(-3.54, -48.96) * mm, "end": v(-2.47, -48.96) * mm});
            skArc(sketch, "E178.2.16", {"start": v(2.47, -48.96) * mm, "mid": v(3.54, -48.96) * mm, "end": v(3.54, -50.03) * mm});
            skLineSegment(sketch, "E178.2.17", {"start": v(2.47, -48.96) * mm, "end": v(0, -51.44) * mm});
            skLineSegment(sketch, "E178.2.18", {"start": v(3.54, -50.03) * mm, "end": v(1.06, -52.5) * mm});
            skLineSegment(sketch, "E178.2.19", {"start": v(-1.5, -24.14) * mm, "end": v(-1.5, -14.14) * mm});
            skArc(sketch, "E178.2.20", {"start": v(1.5, -24.14) * mm, "mid": v(0, -25.64) * mm, "end": v(-1.5, -24.14) * mm});
            skLineSegment(sketch, "E178.2.21", {"start": v(1.5, -24.14) * mm, "end": v(1.5, -14.14) * mm});
            skArc(sketch, "E178.2.22", {"start": v(1.5, -14.14) * mm, "mid": v(0, -12.64) * mm, "end": v(-1.5, -14.14) * mm});
            skLineSegment(sketch, "E178.3.0", {"start": v(49.25, 5.63) * mm, "end": v(17.6, 5.63) * mm});
            skArc(sketch, "E178.3.1", {"start": v(49.25, 5.63) * mm, "mid": v(59, 0) * mm, "end": v(49.25, -5.63) * mm});
            skLineSegment(sketch, "E178.3.2", {"start": v(49.25, -5.63) * mm, "end": v(17.6, -5.63) * mm});
            skArc(sketch, "E178.3.3", {"start": v(42.14, 1.5) * mm, "mid": v(43.64, 0) * mm, "end": v(42.14, -1.5) * mm});
            skLineSegment(sketch, "E178.3.4", {"start": v(42.14, -1.5) * mm, "end": v(32.14, -1.5) * mm});
            skLineSegment(sketch, "E178.3.5", {"start": v(32.14, 1.5) * mm, "end": v(42.14, 1.5) * mm});
            skArc(sketch, "E178.3.6", {"start": v(32.14, 1.5) * mm, "mid": v(30.64, 0) * mm, "end": v(32.14, -1.5) * mm});
            skArc(sketch, "E178.3.7", {"start": v(54.97, 3.54) * mm, "mid": v(56.04, 3.54) * mm, "end": v(56.04, 2.47) * mm});
            skLineSegment(sketch, "E178.3.8", {"start": v(56.04, 2.47) * mm, "end": v(53.56, 0) * mm});
            skLineSegment(sketch, "E178.3.9", {"start": v(54.97, 3.54) * mm, "end": v(52.5, 1.06) * mm});
            skLineSegment(sketch, "E178.3.10", {"start": v(56.04, -2.47) * mm, "end": v(53.56, 0) * mm});
            skLineSegment(sketch, "E178.3.11", {"start": v(54.97, -3.54) * mm, "end": v(52.5, -1.06) * mm});
            skArc(sketch, "E178.3.12", {"start": v(56.04, -2.47) * mm, "mid": v(56.04, -3.54) * mm, "end": v(54.97, -3.54) * mm});
            skLineSegment(sketch, "E178.3.13", {"start": v(50.03, -3.54) * mm, "end": v(52.5, -1.06) * mm});
            skLineSegment(sketch, "E178.3.14", {"start": v(48.96, -2.47) * mm, "end": v(51.44, 0) * mm});
            skArc(sketch, "E178.3.15", {"start": v(50.03, -3.54) * mm, "mid": v(48.96, -3.54) * mm, "end": v(48.96, -2.47) * mm});
            skArc(sketch, "E178.3.16", {"start": v(48.96, 2.47) * mm, "mid": v(48.96, 3.54) * mm, "end": v(50.03, 3.54) * mm});
            skLineSegment(sketch, "E178.3.17", {"start": v(48.96, 2.47) * mm, "end": v(51.44, 0) * mm});
            skLineSegment(sketch, "E178.3.18", {"start": v(50.03, 3.54) * mm, "end": v(52.5, 1.06) * mm});
            skLineSegment(sketch, "E178.3.19", {"start": v(24.14, -1.5) * mm, "end": v(14.14, -1.5) * mm});
            skArc(sketch, "E178.3.20", {"start": v(24.14, 1.5) * mm, "mid": v(25.64, 0) * mm, "end": v(24.14, -1.5) * mm});
            skLineSegment(sketch, "E178.3.21", {"start": v(24.14, 1.5) * mm, "end": v(14.14, 1.5) * mm});
            skArc(sketch, "E178.3.22", {"start": v(14.14, 1.5) * mm, "mid": v(12.64, 0) * mm, "end": v(14.14, -1.5) * mm});
            skLineSegment(sketch, "E179", {"start": v(-8.56, 10.53) * mm, "end": v(-10.53, 8.56) * mm});
            skLineSegment(sketch, "E180", {"start": v(-10.53, -8.56) * mm, "end": v(-8.56, -10.53) * mm});
            skLineSegment(sketch, "E181", {"start": v(8.56, -10.53) * mm, "end": v(10.53, -8.56) * mm});
            skLineSegment(sketch, "E182", {"start": v(10.53, 8.56) * mm, "end": v(8.56, 10.53) * mm});
            skPoint(sketch, "E183.visualSharp", {"position": v(-5.63, 13.46) * mm});
            skArc(sketch, "E183.filletArc", {"start": v(-8.56, 10.53) * mm, "mid": v(-6.4, 13.78) * mm, "end": v(-5.63, 17.6) * mm});
            skPoint(sketch, "E184.visualSharp", {"position": v(-13.46, 5.63) * mm});
            skArc(sketch, "E184.filletArc", {"start": v(-17.6, 5.63) * mm, "mid": v(-13.78, 6.4) * mm, "end": v(-10.53, 8.56) * mm});
            skPoint(sketch, "E185.visualSharp", {"position": v(5.63, 13.46) * mm});
            skArc(sketch, "E185.filletArc", {"start": v(5.63, 17.6) * mm, "mid": v(6.4, 13.78) * mm, "end": v(8.56, 10.53) * mm});
            skPoint(sketch, "E186.visualSharp", {"position": v(13.46, 5.63) * mm});
            skArc(sketch, "E186.filletArc", {"start": v(10.53, 8.56) * mm, "mid": v(13.78, 6.4) * mm, "end": v(17.6, 5.63) * mm});
            skPoint(sketch, "E187.visualSharp", {"position": v(13.46, -5.63) * mm});
            skArc(sketch, "E187.filletArc", {"start": v(17.6, -5.63) * mm, "mid": v(13.78, -6.4) * mm, "end": v(10.53, -8.56) * mm});
            skPoint(sketch, "E188.visualSharp", {"position": v(5.63, -13.46) * mm});
            skArc(sketch, "E188.filletArc", {"start": v(8.56, -10.53) * mm, "mid": v(6.4, -13.78) * mm, "end": v(5.63, -17.6) * mm});
            skPoint(sketch, "E189.visualSharp", {"position": v(-5.63, -13.46) * mm});
            skArc(sketch, "E189.filletArc", {"start": v(-5.63, -17.6) * mm, "mid": v(-6.4, -13.78) * mm, "end": v(-8.56, -10.53) * mm});
            skPoint(sketch, "E190.visualSharp", {"position": v(-13.46, -5.63) * mm});
            skArc(sketch, "E190.filletArc", {"start": v(-10.53, -8.56) * mm, "mid": v(-13.78, -6.4) * mm, "end": v(-17.6, -5.63) * mm});
            skCircle(sketch, "E191", {"center": v(-71.76, -37.23) * mm, "radius": 1.5 * mm});
            skCircle(sketch, "E192.0", {"center": v(-71.76, -37.23) * mm, "radius": 2.7 * mm});
            skSolve(sketch);
        }
        {
            var Q0;
            Q0=makeQuery(id+"F2.imprint","IMPRINT",FACE,{"disambiguationData":[TD([[makeQuery(id+"F2.imprint","IMPRINT",EDGE,{"derivedFrom":sQuery(id+"F2.wireOp",EDGE,"E109")}),-1.0]])]});
            extrude(context, id + "F3", {"entities" : qUnion([Q0]), "depth" : 2 * mm});
        }
        {
            var Q0;
            Q0=makeQuery(id+"F2.imprint","IMPRINT",FACE,{"disambiguationData":[TD([[makeQuery(id+"F2.imprint","IMPRINT",EDGE,{"derivedFrom":sQuery(id+"F2.wireOp",EDGE,"E191")}),-1.0]])]});
            extrude(context, id + "F4", {"entities" : qUnion([Q0]), "depth" : 4 * mm});
        }
    });
